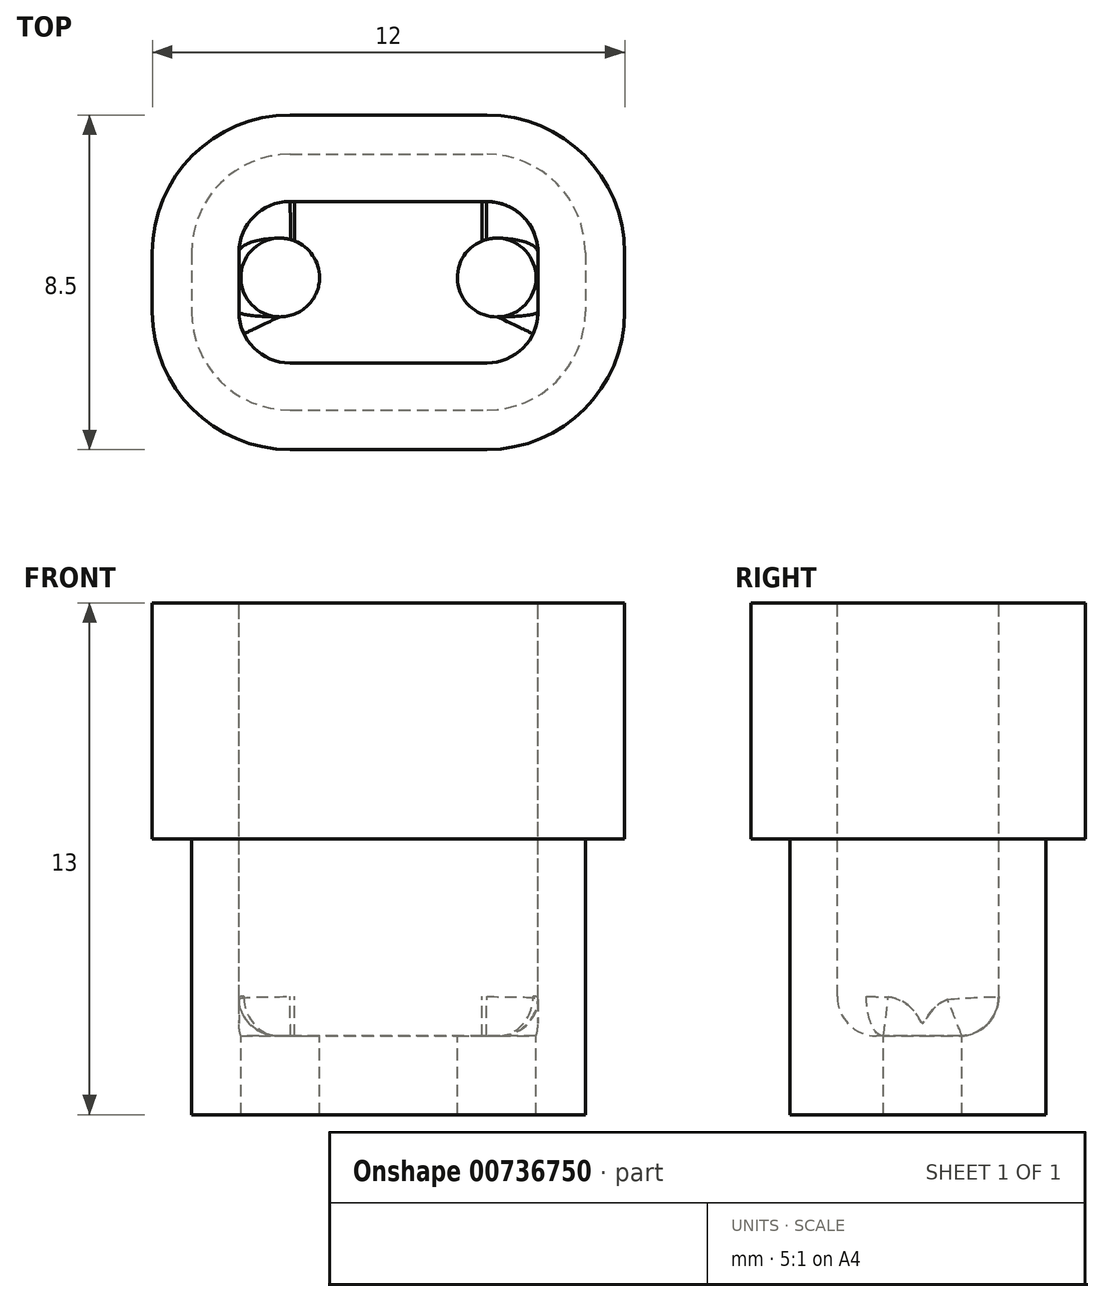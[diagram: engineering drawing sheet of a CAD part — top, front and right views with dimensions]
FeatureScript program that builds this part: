
annotation { "Feature Type Name" : "Feature", "Feature Type Description" : "" }
export const myFeature = defineFeature(function(context is Context, id is Id, definition is map)
    precondition{}
    {
        {
            var Q0;
            Q0=qCreatedBy(makeId("Top.planeOp"),FACE);
            var sketch = newSketch(context, id + "F0", { "sketchPlane" : qUnion([Q0])});
            skLineSegment(sketch, "E0.bottom", {"start": v(-4.81, 3.13) * mm, "end": v(5.19, 3.13) * mm});
            skLineSegment(sketch, "E0.top", {"start": v(-4.81, -3.37) * mm, "end": v(5.19, -3.37) * mm});
            skLineSegment(sketch, "E0.left", {"start": v(-4.81, 3.13) * mm, "end": v(-4.81, -3.37) * mm});
            skLineSegment(sketch, "E0.right", {"start": v(5.19, 3.13) * mm, "end": v(5.19, -3.37) * mm});
            skLineSegment(sketch, "E1", {"start": v(-4.81, 3.13) * mm, "end": v(5.19, -3.37) * mm, "construction": true});
            skLineSegment(sketch, "E2", {"start": v(5.19, 3.13) * mm, "end": v(-4.81, -3.37) * mm, "construction": true});
            skSolve(sketch);
        }
        {
            var Q0;
            Q0 = qSketchRegion(id + "F0", true);
            extrude(context, id + "F1", {"entities" : qUnion([Q0]), "depth" : 7 * mm, "offsetDistance" : 25 * mm});
        }
        {
            var Q0;
            Q0=makeQuery(id+"F1.opExtrude","SWEPT_EDGE",EDGE,{"disambiguationData":[OSD([sQuery(id+"F0.wireOp",EDGE,"E0.bottom"),sQuery(id+"F0.wireOp",EDGE,"E0.right")])]});
            var Q1;
            Q1=makeQuery(id+"F1.opExtrude","SWEPT_EDGE",EDGE,{"disambiguationData":[OSD([sQuery(id+"F0.wireOp",EDGE,"E0.bottom"),sQuery(id+"F0.wireOp",EDGE,"E0.left")])]});
            var Q2;
            Q2=makeQuery(id+"F1.opExtrude","SWEPT_EDGE",EDGE,{"disambiguationData":[OSD([sQuery(id+"F0.wireOp",EDGE,"E0.top"),sQuery(id+"F0.wireOp",EDGE,"E0.left")])]});
            var Q3;
            Q3=makeQuery(id+"F1.opExtrude","SWEPT_EDGE",EDGE,{"disambiguationData":[OSD([sQuery(id+"F0.wireOp",EDGE,"E0.top"),sQuery(id+"F0.wireOp",EDGE,"E0.right")])]});
            fillet(context, id + "F2", {"entities" : qUnion([Q0, Q1, Q2, Q3]), "radius" : 2.5 * mm, "tangentPropagation" : true, "allowEdgeOverflow" : false});
        }
        {
            var Q0;
            Q0=makeQuery(id+"F1.opExtrude","CAP_FACE",FACE,{"disambiguationData":[OSD([sQuery(id+"F0.wireOp",EDGE,"E0.bottom"),sQuery(id+"F0.wireOp",EDGE,"E0.top"),sQuery(id+"F0.wireOp",EDGE,"E0.left"),sQuery(id+"F0.wireOp",EDGE,"E0.right")])],"isStart":false});
            var sketch = newSketch(context, id + "F3", { "sketchPlane" : qUnion([Q0])});
            skCircle(sketch, "E3", {"center": v(2.94, 0) * mm, "radius": 1 * mm});
            skCircle(sketch, "E4", {"center": v(-2.56, 0) * mm, "radius": 1 * mm});
            skLineSegment(sketch, "E5", {"start": v(0.19, -3.37) * mm, "end": v(0.19, 3.13) * mm, "construction": true});
            skSolve(sketch);
        }
        {
            var Q0;
            Q0 = qSketchRegion(id + "F3", true);
            extrude(context, id + "F4", {"entities" : qUnion([Q0]), "operationType" : NewBodyOperationType.REMOVE, "oppositeDirection" : true, "depth" : 25 * mm, "offsetDistance" : 25 * mm});
        }
        {
            var Q0;
            Q0=makeQuery(id+"F1.opExtrude","CAP_FACE",FACE,{"disambiguationData":[OSD([sQuery(id+"F0.wireOp",EDGE,"E0.bottom"),sQuery(id+"F0.wireOp",EDGE,"E0.top"),sQuery(id+"F0.wireOp",EDGE,"E0.left"),sQuery(id+"F0.wireOp",EDGE,"E0.right")])],"isStart":false});
            var sketch = newSketch(context, id + "F5", { "sketchPlane" : qUnion([Q0])});
            skArc(sketch, "E6.0", {"start": v(-2.31, 1.93) * mm, "mid": v(-3.23, 1.55) * mm, "end": v(-3.61, 0.63) * mm});
            skLineSegment(sketch, "E6.1", {"start": v(2.69, 1.93) * mm, "end": v(-2.31, 1.93) * mm});
            skLineSegment(sketch, "E6.2", {"start": v(-3.61, 0.63) * mm, "end": v(-3.61, -0.87) * mm});
            skArc(sketch, "E6.3", {"start": v(3.99, 0.63) * mm, "mid": v(3.6, 1.55) * mm, "end": v(2.69, 1.93) * mm});
            skArc(sketch, "E6.4", {"start": v(-3.61, -0.87) * mm, "mid": v(-3.23, -1.79) * mm, "end": v(-2.31, -2.17) * mm});
            skLineSegment(sketch, "E6.5", {"start": v(-2.31, -2.17) * mm, "end": v(2.69, -2.17) * mm});
            skArc(sketch, "E6.6", {"start": v(2.69, -2.17) * mm, "mid": v(3.6, -1.79) * mm, "end": v(3.99, -0.87) * mm});
            skLineSegment(sketch, "E6.7", {"start": v(3.99, -0.87) * mm, "end": v(3.99, 0.63) * mm});
            skSolve(sketch);
        }
        {
            var Q0;
            Q0 = qSketchRegion(id + "F5", true);
            extrude(context, id + "F6", {"entities" : qUnion([Q0]), "operationType" : NewBodyOperationType.REMOVE, "oppositeDirection" : true, "depth" : 5 * mm, "offsetDistance" : 25 * mm});
        }
        {
            var Q0;
            Q0=makeQuery(id+"F1.opExtrude","CAP_FACE",FACE,{"disambiguationData":[OSD([sQuery(id+"F0.wireOp",EDGE,"E0.bottom"),sQuery(id+"F0.wireOp",EDGE,"E0.top"),sQuery(id+"F0.wireOp",EDGE,"E0.left"),sQuery(id+"F0.wireOp",EDGE,"E0.right")])],"isStart":false});
            var sketch = newSketch(context, id + "F7", { "sketchPlane" : qUnion([Q0])});
            skArc(sketch, "E7.0", {"start": v(-2.31, 4.13) * mm, "mid": v(-4.79, 3.1) * mm, "end": v(-5.81, 0.63) * mm});
            skLineSegment(sketch, "E7.1", {"start": v(2.69, 4.13) * mm, "end": v(-2.31, 4.13) * mm});
            skLineSegment(sketch, "E7.2", {"start": v(-5.81, 0.63) * mm, "end": v(-5.81, -0.87) * mm});
            skArc(sketch, "E7.3", {"start": v(6.19, 0.63) * mm, "mid": v(5.16, 3.1) * mm, "end": v(2.69, 4.13) * mm});
            skArc(sketch, "E7.4", {"start": v(-5.81, -0.87) * mm, "mid": v(-4.79, -3.35) * mm, "end": v(-2.31, -4.37) * mm});
            skLineSegment(sketch, "E7.5", {"start": v(-2.31, -4.37) * mm, "end": v(2.69, -4.37) * mm});
            skArc(sketch, "E7.6", {"start": v(2.69, -4.37) * mm, "mid": v(5.16, -3.35) * mm, "end": v(6.19, -0.87) * mm});
            skLineSegment(sketch, "E7.7", {"start": v(6.19, -0.87) * mm, "end": v(6.19, 0.63) * mm});
            skArc(sketch, "E8.0", {"start": v(-2.31, 1.93) * mm, "mid": v(-3.23, 1.55) * mm, "end": v(-3.61, 0.63) * mm});
            skLineSegment(sketch, "E8.1", {"start": v(2.69, 1.93) * mm, "end": v(-2.31, 1.93) * mm});
            skLineSegment(sketch, "E8.2", {"start": v(-3.61, 0.63) * mm, "end": v(-3.61, -0.87) * mm});
            skArc(sketch, "E8.3", {"start": v(3.99, 0.63) * mm, "mid": v(3.6, 1.55) * mm, "end": v(2.69, 1.93) * mm});
            skArc(sketch, "E8.4", {"start": v(-3.61, -0.87) * mm, "mid": v(-3.23, -1.79) * mm, "end": v(-2.31, -2.17) * mm});
            skLineSegment(sketch, "E8.5", {"start": v(-2.31, -2.17) * mm, "end": v(2.69, -2.17) * mm});
            skArc(sketch, "E8.6", {"start": v(2.69, -2.17) * mm, "mid": v(3.6, -1.79) * mm, "end": v(3.99, -0.87) * mm});
            skLineSegment(sketch, "E8.7", {"start": v(3.99, -0.87) * mm, "end": v(3.99, 0.63) * mm});
            skSolve(sketch);
        }
        {
            var Q0;
            Q0 = qSketchRegion(id + "F7", true);
            extrude(context, id + "F8", {"entities" : qUnion([Q0]), "operationType" : NewBodyOperationType.ADD, "depth" : 6 * mm, "offsetDistance" : 25 * mm});
        }
        {
            var Q0;
            Q0=makeQuery(id+"F6.boolean.opBoolean","COPY",EDGE,{"derivedFrom":makeQuery(id+"F6.opExtrude","CAP_EDGE",EDGE,{"disambiguationData":[OSD([sQuery(id+"F5.wireOp",EDGE,"E6.5")])],"isStart":false})});
            fillet(context, id + "F9", {"entities" : qUnion([Q0]), "radius" : 1 * mm, "tangentPropagation" : true, "allowEdgeOverflow" : false});
        }
    });
